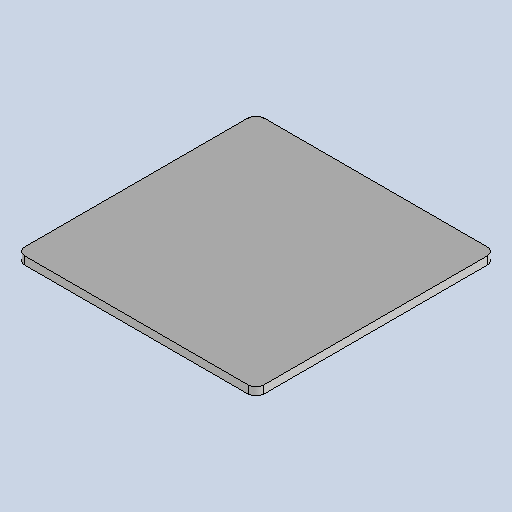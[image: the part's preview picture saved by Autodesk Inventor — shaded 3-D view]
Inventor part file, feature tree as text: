
AUTODESK INVENTOR PART (.ipt)
format: ipt  version: 2025.1 (Build 291241020, 241B)  size: 143,872 bytes
history: native  units: mm
features: other x2, sheet_metal_op x1, chamfer x1, sketch x1
ambient origin geometry x8: Origin, YZ Plane, XZ Plane, XY Plane, X Axis, Y Axis, Z Axis, Center Point
bodies: Body1 (feature_tree)
feature tree (5):
  sheet_metal_op  "Face3"
  chamfer  "Corner Round1"
  sketch  "Sketch1"  dims[d154=60.0mm d155=60.0mm d156=2.0mm d172=30.5mm d178=2.0mm]
  other  "Plate5"
  other  "Definition1"
